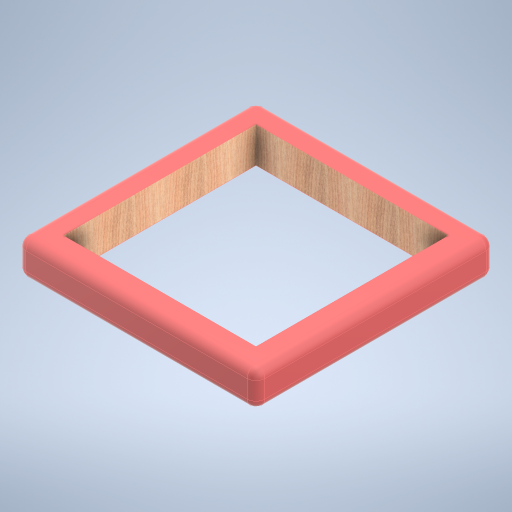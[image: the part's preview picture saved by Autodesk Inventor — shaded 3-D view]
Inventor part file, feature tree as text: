
AUTODESK INVENTOR PART (.ipt)
format: ipt  version: 2024.2 (Build 282272000, 272)  size: 352,768 bytes
history: native  units: in
note: dims shown in document units (in); Inventor stores cm internally (conversion verified against a paired STEP export)
features: extrude x5, fillet x1, other x1
ambient origin geometry x8: Origin, YZ Plane, XZ Plane, XY Plane, X Axis, Y Axis, Z Axis, Center Point
bodies: Solid1 (feature_tree)
feature tree (7):
  extrude  "Extrusion1"  Depth=3.25in
  fillet  "Fillet1"  Radius=3.25in
  other  "Bumper_Gaps"
  extrude  "Front_Gap"  Depth=27.0in
  extrude  "Back_Gap"  Depth=27.0in
  extrude  "Left_Gap"  Depth=5.0in TaperAngle=0.0deg
  extrude  "Right_Gap"  Depth=1.25in
